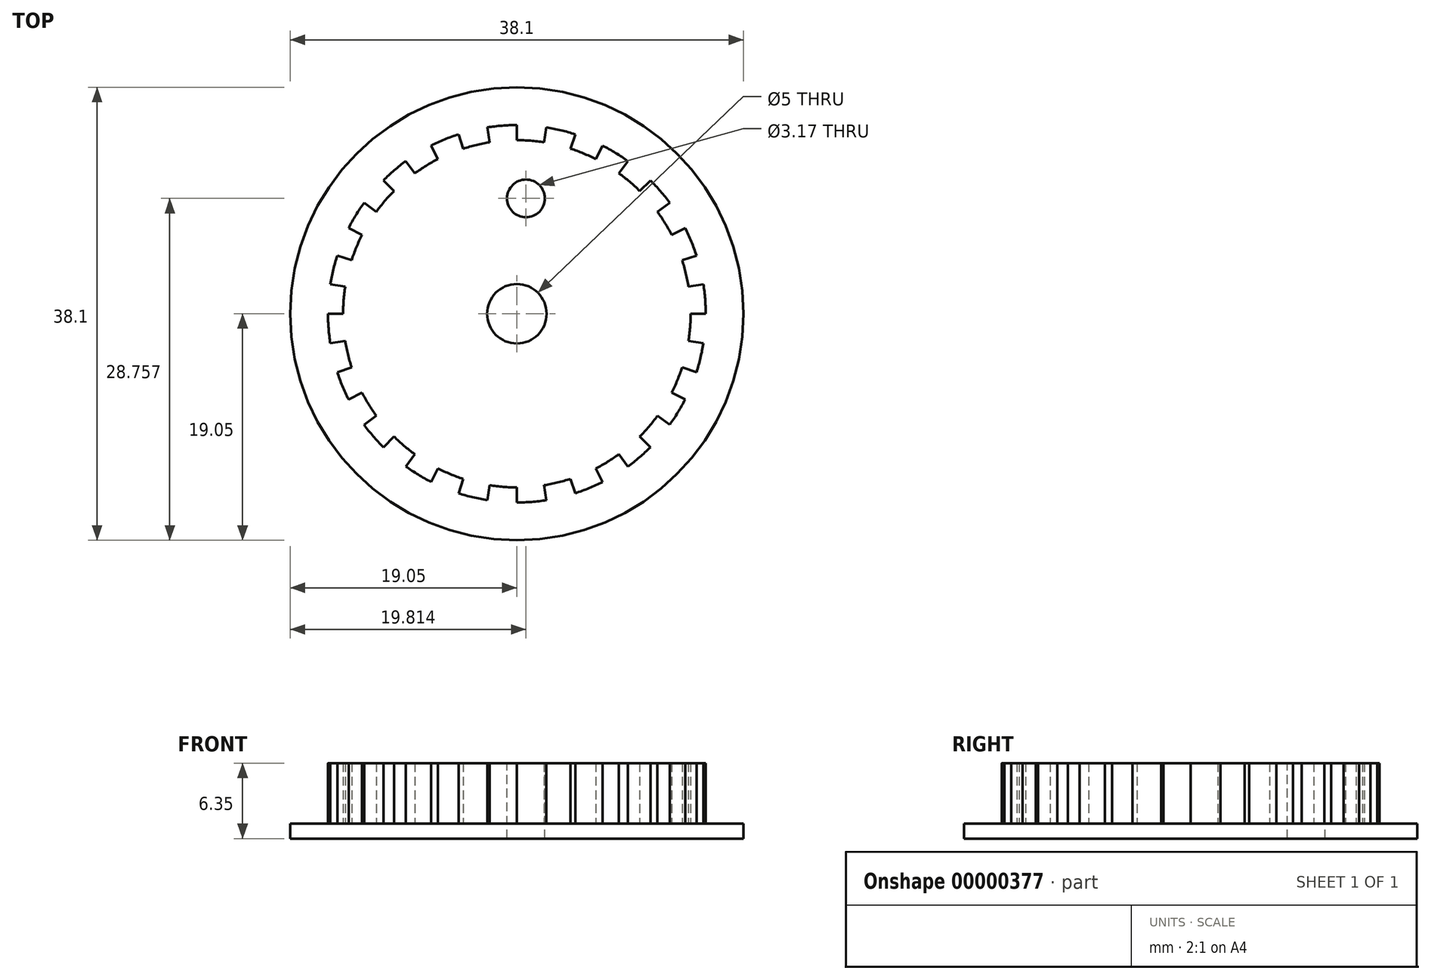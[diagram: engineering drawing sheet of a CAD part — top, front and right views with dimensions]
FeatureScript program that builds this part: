
annotation { "Feature Type Name" : "Feature", "Feature Type Description" : "" }
export const myFeature = defineFeature(function(context is Context, id is Id, definition is map)
    precondition{}
    {
        {
            var Q0;
            Q0 = qCreatedBy(makeId("Top.planeOp"), FACE);
            var sketch = newSketch(context, id + "F0", { "sketchPlane" : qUnion([Q0])});
            skCircle(sketch, "E0", {"center": v(0, 0) * mm, "radius": 19.05 * mm});
            skCircle(sketch, "E1", {"center": v(0, 0) * mm, "radius": 2.5 * mm});
            skSolve(sketch);
        }
        {
            var Q0;
            Q0=makeQuery(id+"F0.imprint","IMPRINT",FACE,{"disambiguationData":[TD([[makeQuery(id+"F0.imprint","IMPRINT",EDGE,{"derivedFrom":sQuery(id+"F0.wireOp",EDGE,"E0")}),1.0]])]});
            extrude(context, id + "F1", {"entities" : qUnion([Q0]), "depth" : 1.27 * mm});
        }
        {
            var Q0;
            Q0=makeQuery(id+"F1.opExtrude","CAP_FACE",FACE,{"disambiguationData":[OSD([sQuery(id+"F0.wireOp",EDGE,"E0"),sQuery(id+"F0.wireOp",EDGE,"E1")])],"isStart":false});
            var sketch = newSketch(context, id + "F2", { "sketchPlane" : qUnion([Q0])});
            skCircle(sketch, "E2", {"center": v(0, 0) * mm, "radius": 14.6 * mm, "construction": true});
            skCircle(sketch, "E3", {"center": v(0, 0) * mm, "radius": 15.88 * mm, "construction": true});
            skLineSegment(sketch, "E4", {"start": v(0, 0) * mm, "end": v(0, 15.88) * mm, "construction": true});
            skLineSegment(sketch, "E5", {"start": v(0, 0) * mm, "end": v(2.48, 15.68) * mm, "construction": true});
            skLineSegment(sketch, "E6", {"start": v(0, 0) * mm, "end": v(4.9, 15.1) * mm, "construction": true});
            skArc(sketch, "E7", {"start": v(2.28, 14.43) * mm, "mid": v(1.15, 14.56) * mm, "end": v(0, 14.6) * mm});
            skLineSegment(sketch, "E8", {"start": v(2.48, 15.68) * mm, "end": v(2.28, 14.43) * mm});
            skArc(sketch, "E9", {"start": v(4.9, 15.1) * mm, "mid": v(3.7, 15.44) * mm, "end": v(2.48, 15.68) * mm});
            skLineSegment(sketch, "E10", {"start": v(0, 14.6) * mm, "end": v(0, 0) * mm});
            skLineSegment(sketch, "E11", {"start": v(4.9, 15.1) * mm, "end": v(0, 0) * mm});
            skSolve(sketch);
        }
        {
            var Q0;
            {var subQ6=sQuery(id+"F2.wireOp",EDGE,"E7");Q0=makeQuery(id+"F2.imprint","IMPRINT",FACE,{"disambiguationData":[TD([[makeQuery(id+"F2.imprint","IMPRINT",EDGE,{"derivedFrom":subQ6}),1.0]])]});}
            var Q1;
            Q1=sQuery(id+"F2.wireOp",EDGE,"E10");
            var Q2;
            Q2=sQuery(id+"F2.wireOp",EDGE,"E7");
            var Q3;
            Q3=sQuery(id+"F2.wireOp",EDGE,"E8");
            var Q4;
            Q4=sQuery(id+"F2.wireOp",EDGE,"E9");
            var Q5;
            Q5=sQuery(id+"F2.wireOp",EDGE,"E11");
            extrude(context, id + "F3", {"entities" : qUnion([Q0]), "surfaceEntities" : qUnion([Q1, Q2, Q3, Q4, Q5]), "depth" : 5.08 * mm});
        }
        {
            var Q0;
            Q0 = qCreatedBy(makeId("Front.planeOp"), FACE);
            var sketch = newSketch(context, id + "F4", { "sketchPlane" : qUnion([Q0])});
            skLineSegment(sketch, "E12", {"start": v(0, 0) * mm, "end": v(0, 20.74) * mm, "construction": true});
            skSolve(sketch);
        }
        {
            var Q0;
            Q0=makeQuery(id+"F3.opExtrude","SWEPT_BODY",BODY,{"disambiguationData":[OSD([sQuery(id+"F0.wireOp",EDGE,"E1"),sQuery(id+"F2.wireOp",EDGE,"E7"),sQuery(id+"F2.wireOp",EDGE,"E8"),sQuery(id+"F2.wireOp",EDGE,"E9"),sQuery(id+"F2.wireOp",EDGE,"E10"),sQuery(id+"F2.wireOp",EDGE,"E11")])]});
            var Q1;
            Q1=sQuery(id+"F4.wireOp",EDGE,"E12");
            circularPattern(context, id + "F5", {"entities" : qUnion([Q0]), "axis" : qUnion([Q1]), "angle" : 18 * degree, "instanceCount" : 20});
        }
        {
            var Q0;
            Q0=makeQuery(id+"F1.opExtrude","SWEPT_BODY",BODY,{"disambiguationData":[OSD([sQuery(id+"F0.wireOp",EDGE,"E0"),sQuery(id+"F0.wireOp",EDGE,"E1")])]});
            var Q1;
            Q1=makeQuery(id+"F5.opPattern","COPY",BODY,{"derivedFrom":makeQuery(id+"F3.opExtrude","SWEPT_BODY",BODY,{"disambiguationData":[OSD([sQuery(id+"F0.wireOp",EDGE,"E1"),sQuery(id+"F2.wireOp",EDGE,"E7"),sQuery(id+"F2.wireOp",EDGE,"E8"),sQuery(id+"F2.wireOp",EDGE,"E9"),sQuery(id+"F2.wireOp",EDGE,"E10"),sQuery(id+"F2.wireOp",EDGE,"E11")])]}),"instanceName":"4"});
            var Q2;
            Q2=makeQuery(id+"F5.opPattern","COPY",BODY,{"derivedFrom":makeQuery(id+"F3.opExtrude","SWEPT_BODY",BODY,{"disambiguationData":[OSD([sQuery(id+"F0.wireOp",EDGE,"E1"),sQuery(id+"F2.wireOp",EDGE,"E7"),sQuery(id+"F2.wireOp",EDGE,"E8"),sQuery(id+"F2.wireOp",EDGE,"E9"),sQuery(id+"F2.wireOp",EDGE,"E10"),sQuery(id+"F2.wireOp",EDGE,"E11")])]}),"instanceName":"3"});
            var Q3;
            Q3=makeQuery(id+"F5.opPattern","COPY",BODY,{"derivedFrom":makeQuery(id+"F3.opExtrude","SWEPT_BODY",BODY,{"disambiguationData":[OSD([sQuery(id+"F0.wireOp",EDGE,"E1"),sQuery(id+"F2.wireOp",EDGE,"E7"),sQuery(id+"F2.wireOp",EDGE,"E8"),sQuery(id+"F2.wireOp",EDGE,"E9"),sQuery(id+"F2.wireOp",EDGE,"E10"),sQuery(id+"F2.wireOp",EDGE,"E11")])]}),"instanceName":"2"});
            var Q4;
            Q4=makeQuery(id+"F5.opPattern","COPY",BODY,{"derivedFrom":makeQuery(id+"F3.opExtrude","SWEPT_BODY",BODY,{"disambiguationData":[OSD([sQuery(id+"F0.wireOp",EDGE,"E1"),sQuery(id+"F2.wireOp",EDGE,"E7"),sQuery(id+"F2.wireOp",EDGE,"E8"),sQuery(id+"F2.wireOp",EDGE,"E9"),sQuery(id+"F2.wireOp",EDGE,"E10"),sQuery(id+"F2.wireOp",EDGE,"E11")])]}),"instanceName":"1"});
            var Q5;
            Q5=makeQuery(id+"F3.opExtrude","SWEPT_BODY",BODY,{"disambiguationData":[OSD([sQuery(id+"F0.wireOp",EDGE,"E1"),sQuery(id+"F2.wireOp",EDGE,"E7"),sQuery(id+"F2.wireOp",EDGE,"E8"),sQuery(id+"F2.wireOp",EDGE,"E9"),sQuery(id+"F2.wireOp",EDGE,"E10"),sQuery(id+"F2.wireOp",EDGE,"E11")])]});
            var Q6;
            Q6=makeQuery(id+"F5.opPattern","COPY",BODY,{"derivedFrom":makeQuery(id+"F3.opExtrude","SWEPT_BODY",BODY,{"disambiguationData":[OSD([sQuery(id+"F0.wireOp",EDGE,"E1"),sQuery(id+"F2.wireOp",EDGE,"E7"),sQuery(id+"F2.wireOp",EDGE,"E8"),sQuery(id+"F2.wireOp",EDGE,"E9"),sQuery(id+"F2.wireOp",EDGE,"E10"),sQuery(id+"F2.wireOp",EDGE,"E11")])]}),"instanceName":"19"});
            var Q7;
            Q7=makeQuery(id+"F5.opPattern","COPY",BODY,{"derivedFrom":makeQuery(id+"F3.opExtrude","SWEPT_BODY",BODY,{"disambiguationData":[OSD([sQuery(id+"F0.wireOp",EDGE,"E1"),sQuery(id+"F2.wireOp",EDGE,"E7"),sQuery(id+"F2.wireOp",EDGE,"E8"),sQuery(id+"F2.wireOp",EDGE,"E9"),sQuery(id+"F2.wireOp",EDGE,"E10"),sQuery(id+"F2.wireOp",EDGE,"E11")])]}),"instanceName":"18"});
            var Q8;
            Q8=makeQuery(id+"F5.opPattern","COPY",BODY,{"derivedFrom":makeQuery(id+"F3.opExtrude","SWEPT_BODY",BODY,{"disambiguationData":[OSD([sQuery(id+"F0.wireOp",EDGE,"E1"),sQuery(id+"F2.wireOp",EDGE,"E7"),sQuery(id+"F2.wireOp",EDGE,"E8"),sQuery(id+"F2.wireOp",EDGE,"E9"),sQuery(id+"F2.wireOp",EDGE,"E10"),sQuery(id+"F2.wireOp",EDGE,"E11")])]}),"instanceName":"17"});
            var Q9;
            Q9=makeQuery(id+"F5.opPattern","COPY",BODY,{"derivedFrom":makeQuery(id+"F3.opExtrude","SWEPT_BODY",BODY,{"disambiguationData":[OSD([sQuery(id+"F0.wireOp",EDGE,"E1"),sQuery(id+"F2.wireOp",EDGE,"E7"),sQuery(id+"F2.wireOp",EDGE,"E8"),sQuery(id+"F2.wireOp",EDGE,"E9"),sQuery(id+"F2.wireOp",EDGE,"E10"),sQuery(id+"F2.wireOp",EDGE,"E11")])]}),"instanceName":"16"});
            var Q10;
            Q10=makeQuery(id+"F5.opPattern","COPY",BODY,{"derivedFrom":makeQuery(id+"F3.opExtrude","SWEPT_BODY",BODY,{"disambiguationData":[OSD([sQuery(id+"F0.wireOp",EDGE,"E1"),sQuery(id+"F2.wireOp",EDGE,"E7"),sQuery(id+"F2.wireOp",EDGE,"E8"),sQuery(id+"F2.wireOp",EDGE,"E9"),sQuery(id+"F2.wireOp",EDGE,"E10"),sQuery(id+"F2.wireOp",EDGE,"E11")])]}),"instanceName":"15"});
            var Q11;
            Q11=makeQuery(id+"F5.opPattern","COPY",BODY,{"derivedFrom":makeQuery(id+"F3.opExtrude","SWEPT_BODY",BODY,{"disambiguationData":[OSD([sQuery(id+"F0.wireOp",EDGE,"E1"),sQuery(id+"F2.wireOp",EDGE,"E7"),sQuery(id+"F2.wireOp",EDGE,"E8"),sQuery(id+"F2.wireOp",EDGE,"E9"),sQuery(id+"F2.wireOp",EDGE,"E10"),sQuery(id+"F2.wireOp",EDGE,"E11")])]}),"instanceName":"14"});
            var Q12;
            Q12=makeQuery(id+"F5.opPattern","COPY",BODY,{"derivedFrom":makeQuery(id+"F3.opExtrude","SWEPT_BODY",BODY,{"disambiguationData":[OSD([sQuery(id+"F0.wireOp",EDGE,"E1"),sQuery(id+"F2.wireOp",EDGE,"E7"),sQuery(id+"F2.wireOp",EDGE,"E8"),sQuery(id+"F2.wireOp",EDGE,"E9"),sQuery(id+"F2.wireOp",EDGE,"E10"),sQuery(id+"F2.wireOp",EDGE,"E11")])]}),"instanceName":"13"});
            var Q13;
            Q13=makeQuery(id+"F5.opPattern","COPY",BODY,{"derivedFrom":makeQuery(id+"F3.opExtrude","SWEPT_BODY",BODY,{"disambiguationData":[OSD([sQuery(id+"F0.wireOp",EDGE,"E1"),sQuery(id+"F2.wireOp",EDGE,"E7"),sQuery(id+"F2.wireOp",EDGE,"E8"),sQuery(id+"F2.wireOp",EDGE,"E9"),sQuery(id+"F2.wireOp",EDGE,"E10"),sQuery(id+"F2.wireOp",EDGE,"E11")])]}),"instanceName":"12"});
            var Q14;
            Q14=makeQuery(id+"F5.opPattern","COPY",BODY,{"derivedFrom":makeQuery(id+"F3.opExtrude","SWEPT_BODY",BODY,{"disambiguationData":[OSD([sQuery(id+"F0.wireOp",EDGE,"E1"),sQuery(id+"F2.wireOp",EDGE,"E7"),sQuery(id+"F2.wireOp",EDGE,"E8"),sQuery(id+"F2.wireOp",EDGE,"E9"),sQuery(id+"F2.wireOp",EDGE,"E10"),sQuery(id+"F2.wireOp",EDGE,"E11")])]}),"instanceName":"11"});
            var Q15;
            Q15=makeQuery(id+"F5.opPattern","COPY",BODY,{"derivedFrom":makeQuery(id+"F3.opExtrude","SWEPT_BODY",BODY,{"disambiguationData":[OSD([sQuery(id+"F0.wireOp",EDGE,"E1"),sQuery(id+"F2.wireOp",EDGE,"E7"),sQuery(id+"F2.wireOp",EDGE,"E8"),sQuery(id+"F2.wireOp",EDGE,"E9"),sQuery(id+"F2.wireOp",EDGE,"E10"),sQuery(id+"F2.wireOp",EDGE,"E11")])]}),"instanceName":"10"});
            var Q16;
            Q16=makeQuery(id+"F5.opPattern","COPY",BODY,{"derivedFrom":makeQuery(id+"F3.opExtrude","SWEPT_BODY",BODY,{"disambiguationData":[OSD([sQuery(id+"F0.wireOp",EDGE,"E1"),sQuery(id+"F2.wireOp",EDGE,"E7"),sQuery(id+"F2.wireOp",EDGE,"E8"),sQuery(id+"F2.wireOp",EDGE,"E9"),sQuery(id+"F2.wireOp",EDGE,"E10"),sQuery(id+"F2.wireOp",EDGE,"E11")])]}),"instanceName":"9"});
            var Q17;
            Q17=makeQuery(id+"F5.opPattern","COPY",BODY,{"derivedFrom":makeQuery(id+"F3.opExtrude","SWEPT_BODY",BODY,{"disambiguationData":[OSD([sQuery(id+"F0.wireOp",EDGE,"E1"),sQuery(id+"F2.wireOp",EDGE,"E7"),sQuery(id+"F2.wireOp",EDGE,"E8"),sQuery(id+"F2.wireOp",EDGE,"E9"),sQuery(id+"F2.wireOp",EDGE,"E10"),sQuery(id+"F2.wireOp",EDGE,"E11")])]}),"instanceName":"8"});
            var Q18;
            Q18=makeQuery(id+"F5.opPattern","COPY",BODY,{"derivedFrom":makeQuery(id+"F3.opExtrude","SWEPT_BODY",BODY,{"disambiguationData":[OSD([sQuery(id+"F0.wireOp",EDGE,"E1"),sQuery(id+"F2.wireOp",EDGE,"E7"),sQuery(id+"F2.wireOp",EDGE,"E8"),sQuery(id+"F2.wireOp",EDGE,"E9"),sQuery(id+"F2.wireOp",EDGE,"E10"),sQuery(id+"F2.wireOp",EDGE,"E11")])]}),"instanceName":"7"});
            var Q19;
            Q19=makeQuery(id+"F5.opPattern","COPY",BODY,{"derivedFrom":makeQuery(id+"F3.opExtrude","SWEPT_BODY",BODY,{"disambiguationData":[OSD([sQuery(id+"F0.wireOp",EDGE,"E1"),sQuery(id+"F2.wireOp",EDGE,"E7"),sQuery(id+"F2.wireOp",EDGE,"E8"),sQuery(id+"F2.wireOp",EDGE,"E9"),sQuery(id+"F2.wireOp",EDGE,"E10"),sQuery(id+"F2.wireOp",EDGE,"E11")])]}),"instanceName":"6"});
            var Q20;
            Q20=makeQuery(id+"F5.opPattern","COPY",BODY,{"derivedFrom":makeQuery(id+"F3.opExtrude","SWEPT_BODY",BODY,{"disambiguationData":[OSD([sQuery(id+"F0.wireOp",EDGE,"E1"),sQuery(id+"F2.wireOp",EDGE,"E7"),sQuery(id+"F2.wireOp",EDGE,"E8"),sQuery(id+"F2.wireOp",EDGE,"E9"),sQuery(id+"F2.wireOp",EDGE,"E10"),sQuery(id+"F2.wireOp",EDGE,"E11")])]}),"instanceName":"5"});
            booleanBodies(context, id + "F6", {"operationType" : BooleanOperationType.UNION, "tools" : qUnion([Q0, Q1, Q2, Q3, Q4, Q5, Q6, Q7, Q8, Q9, Q10, Q11, Q12, Q13, Q14, Q15, Q16, Q17, Q18, Q19, Q20])});
        }
        {
            var Q0;
            {var subQ0=makeQuery(id+"F3.opExtrude","CAP_FACE",FACE,{"disambiguationData":[OSD([sQuery(id+"F0.wireOp",EDGE,"E1"),sQuery(id+"F2.wireOp",EDGE,"E7"),sQuery(id+"F2.wireOp",EDGE,"E8"),sQuery(id+"F2.wireOp",EDGE,"E9"),sQuery(id+"F2.wireOp",EDGE,"E10"),sQuery(id+"F2.wireOp",EDGE,"E11")])],"isStart":false});Q0=makeQuery(id+"F6.opBoolean","MERGE",FACE,{"derivedFrom":[subQ0,makeQuery(id+"F5.opPattern","COPY",FACE,{"derivedFrom":subQ0,"instanceName":"1"}),makeQuery(id+"F5.opPattern","COPY",FACE,{"derivedFrom":subQ0,"instanceName":"2"}),makeQuery(id+"F5.opPattern","COPY",FACE,{"derivedFrom":subQ0,"instanceName":"3"}),makeQuery(id+"F5.opPattern","COPY",FACE,{"derivedFrom":subQ0,"instanceName":"4"}),makeQuery(id+"F5.opPattern","COPY",FACE,{"derivedFrom":subQ0,"instanceName":"5"}),makeQuery(id+"F5.opPattern","COPY",FACE,{"derivedFrom":subQ0,"instanceName":"6"}),makeQuery(id+"F5.opPattern","COPY",FACE,{"derivedFrom":subQ0,"instanceName":"7"}),makeQuery(id+"F5.opPattern","COPY",FACE,{"derivedFrom":subQ0,"instanceName":"8"}),makeQuery(id+"F5.opPattern","COPY",FACE,{"derivedFrom":subQ0,"instanceName":"9"}),makeQuery(id+"F5.opPattern","COPY",FACE,{"derivedFrom":subQ0,"instanceName":"10"}),makeQuery(id+"F5.opPattern","COPY",FACE,{"derivedFrom":subQ0,"instanceName":"11"}),makeQuery(id+"F5.opPattern","COPY",FACE,{"derivedFrom":subQ0,"instanceName":"12"}),makeQuery(id+"F5.opPattern","COPY",FACE,{"derivedFrom":subQ0,"instanceName":"13"}),makeQuery(id+"F5.opPattern","COPY",FACE,{"derivedFrom":subQ0,"instanceName":"14"}),makeQuery(id+"F5.opPattern","COPY",FACE,{"derivedFrom":subQ0,"instanceName":"15"}),makeQuery(id+"F5.opPattern","COPY",FACE,{"derivedFrom":subQ0,"instanceName":"16"}),makeQuery(id+"F5.opPattern","COPY",FACE,{"derivedFrom":subQ0,"instanceName":"17"}),makeQuery(id+"F5.opPattern","COPY",FACE,{"derivedFrom":subQ0,"instanceName":"18"}),makeQuery(id+"F5.opPattern","COPY",FACE,{"derivedFrom":subQ0,"instanceName":"19"})]});}
            var sketch = newSketch(context, id + "F7", { "sketchPlane" : qUnion([Q0])});
            skCircle(sketch, "E13", {"center": v(0.76, 9.7) * mm, "radius": 1.59 * mm});
            skLineSegment(sketch, "E14", {"start": v(0, 0) * mm, "end": v(0.38, 4.85) * mm, "construction": true});
            skLineSegment(sketch, "E15", {"start": v(0.38, 4.85) * mm, "end": v(0.76, 9.7) * mm, "construction": true});
            skLineSegment(sketch, "E16", {"start": v(0.76, 9.7) * mm, "end": v(1.15, 14.56) * mm, "construction": true});
            skSolve(sketch);
        }
        {
            var Q0;
            Q0=makeQuery(id+"F7.imprint","IMPRINT",FACE,{"disambiguationData":[TD([[makeQuery(id+"F7.imprint","IMPRINT",EDGE,{"derivedFrom":sQuery(id+"F7.wireOp",EDGE,"E13")}),1.0]])]});
            extrude(context, id + "F8", {"entities" : qUnion([Q0]), "operationType" : NewBodyOperationType.REMOVE, "oppositeDirection" : true, "depth" : 6.35 * mm});
        }
    });
